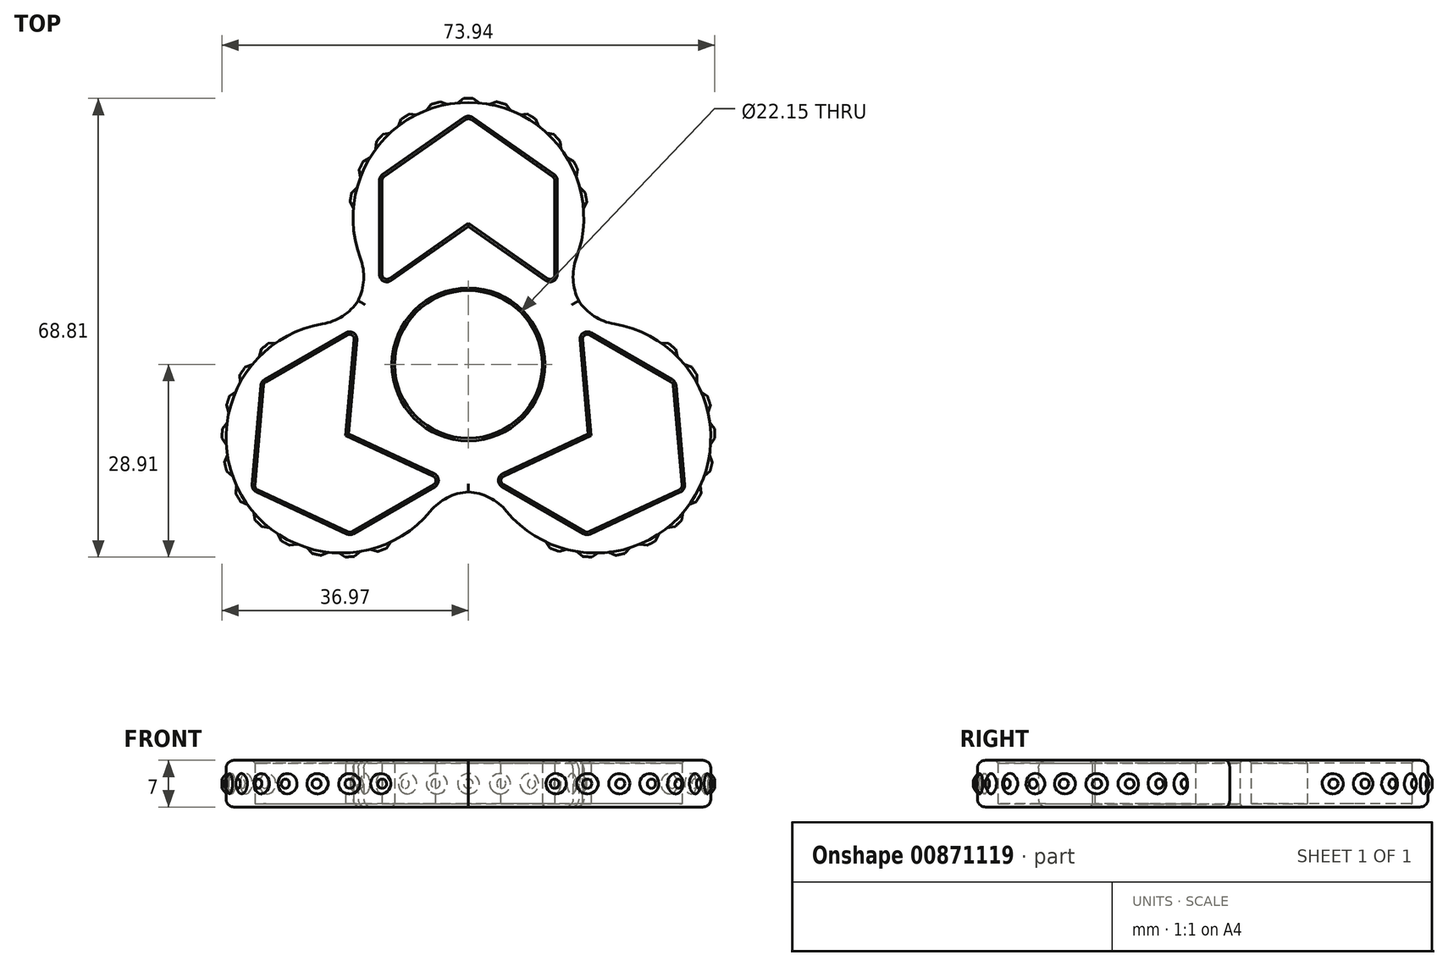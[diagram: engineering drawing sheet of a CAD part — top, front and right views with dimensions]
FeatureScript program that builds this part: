
annotation { "Feature Type Name" : "Feature", "Feature Type Description" : "" }
export const myFeature = defineFeature(function(context is Context, id is Id, definition is map)
    precondition{}
    {
        {
            var Q0;
            Q0=qCreatedBy(makeId("Top.planeOp"),FACE);
            var sketch = newSketch(context, id + "F0", { "sketchPlane" : qUnion([Q0])});
            skCircle(sketch, "E0", {"center": v(0, 0) * mm, "radius": 11.07 * mm});
            skCircle(sketch, "E1", {"center": v(0, 0) * mm, "radius": 26.5 * mm, "construction": true});
            skArc(sketch, "E2", {"start": v(-13.1, 23.03) * mm, "mid": v(-13.03, 22.75) * mm, "end": v(-12.95, 22.47) * mm, "construction": true});
            skLineSegment(sketch, "E3", {"start": v(0, 43.45) * mm, "end": v(0, 0) * mm});
            skLineSegment(sketch, "E4", {"start": v(0, 37) * mm, "end": v(12.95, 27.94) * mm});
            skLineSegment(sketch, "E5", {"start": v(12.95, 27.94) * mm, "end": v(12.95, 12.13) * mm});
            skLineSegment(sketch, "E6", {"start": v(12.95, 12.13) * mm, "end": v(0, 21.2) * mm});
            skLineSegment(sketch, "E7.MirrorCS", {"start": v(0, 37) * mm, "end": v(-12.95, 27.94) * mm});
            skLineSegment(sketch, "E8.MirrorCS", {"start": v(-12.95, 27.94) * mm, "end": v(-12.95, 12.13) * mm});
            skLineSegment(sketch, "E9.MirrorCS", {"start": v(-12.95, 12.13) * mm, "end": v(0, 21.2) * mm});
            skLineSegment(sketch, "E10.1.0", {"start": v(-32.1, -18.57) * mm, "end": v(-17.76, -25.25) * mm});
            skLineSegment(sketch, "E10.1.1", {"start": v(-17.76, -25.25) * mm, "end": v(-4.07, -17.35) * mm});
            skLineSegment(sketch, "E10.1.2", {"start": v(-4.07, -17.35) * mm, "end": v(-18.4, -10.67) * mm});
            skLineSegment(sketch, "E10.1.3", {"start": v(-17.02, 5.08) * mm, "end": v(-18.4, -10.67) * mm});
            skLineSegment(sketch, "E10.1.4", {"start": v(-30.71, -2.82) * mm, "end": v(-17.02, 5.08) * mm});
            skLineSegment(sketch, "E10.1.5", {"start": v(-32.1, -18.57) * mm, "end": v(-30.71, -2.82) * mm});
            skLineSegment(sketch, "E10.2.0", {"start": v(32.1, -18.57) * mm, "end": v(30.71, -2.82) * mm});
            skLineSegment(sketch, "E10.2.1", {"start": v(30.71, -2.82) * mm, "end": v(17.02, 5.08) * mm});
            skLineSegment(sketch, "E10.2.2", {"start": v(17.02, 5.08) * mm, "end": v(18.4, -10.67) * mm});
            skLineSegment(sketch, "E10.2.3", {"start": v(4.07, -17.35) * mm, "end": v(18.4, -10.67) * mm});
            skLineSegment(sketch, "E10.2.4", {"start": v(17.76, -25.25) * mm, "end": v(4.07, -17.35) * mm});
            skLineSegment(sketch, "E10.2.5", {"start": v(32.1, -18.57) * mm, "end": v(17.76, -25.25) * mm});
            skPoint(sketch, "E10.center", {"position": v(0, -0.05) * mm});
            skArc(sketch, "E11.trimOffspring", {"start": v(12.95, 22.47) * mm, "mid": v(13, 22.77) * mm, "end": v(13.05, 23.06) * mm, "construction": true});
            skCircle(sketch, "E12", {"center": v(0, 22) * mm, "radius": 17.3 * mm});
            skCircle(sketch, "E13.1.0", {"center": v(-19.05, -11) * mm, "radius": 17.3 * mm});
            skCircle(sketch, "E13.2.0", {"center": v(19.05, -11) * mm, "radius": 17.3 * mm});
            skLineSegment(sketch, "E14", {"start": v(-17.02, 5.08) * mm, "end": v(-12.95, 12.13) * mm});
            skLineSegment(sketch, "E15", {"start": v(12.95, 12.13) * mm, "end": v(17.02, 5.08) * mm});
            skLineSegment(sketch, "E16", {"start": v(4.07, -17.35) * mm, "end": v(-4.07, -17.35) * mm});
            skLineSegment(sketch, "E17", {"start": v(-7.18, -19.14) * mm, "end": v(7.18, -19.14) * mm});
            skLineSegment(sketch, "E18.1.0", {"start": v(20.13, 3.3) * mm, "end": v(12.96, 15.73) * mm});
            skLineSegment(sketch, "E18.2.0", {"start": v(-12.96, 15.73) * mm, "end": v(-20.13, 3.3) * mm});
            skPoint(sketch, "E18.center", {"position": v(0, -0.03) * mm});
            skSolve(sketch);
        }
        {
            var Q0;
            {var subQ1=sQuery(id+"F0.wireOp",EDGE,"E7.MirrorCS");Q0=makeQuery(id+"F0.imprint","IMPRINT",FACE,{"disambiguationData":[TD([[makeQuery(id+"F0.imprint","IMPRINT",EDGE,{"derivedFrom":subQ1}),-1.0]])]});}
            var Q1;
            {var subQ0=sQuery(id+"F0.wireOp",EDGE,"E4");Q1=makeQuery(id+"F0.imprint","IMPRINT",FACE,{"disambiguationData":[TD([[makeQuery(id+"F0.imprint","IMPRINT",EDGE,{"derivedFrom":subQ0}),1.0]])]});}
            var Q2;
            {var subQ5=sQuery(id+"F0.wireOp",EDGE,"E6");Q2=makeQuery(id+"F0.imprint","IMPRINT",FACE,{"disambiguationData":[TD([[makeQuery(id+"F0.imprint","IMPRINT",EDGE,{"derivedFrom":subQ5}),1.0]])]});}
            var Q3;
            {var subQ0=sQuery(id+"F0.wireOp",EDGE,"E9.MirrorCS");Q3=makeQuery(id+"F0.imprint","IMPRINT",FACE,{"disambiguationData":[TD([[makeQuery(id+"F0.imprint","IMPRINT",EDGE,{"derivedFrom":subQ0}),-1.0]])]});}
            var Q4;
            {var subQ0=sQuery(id+"F0.wireOp",EDGE,"E12");var subQ1=sQuery(id+"F0.wireOp",EDGE,"E0");var subQ2=makeQuery(id+"F0.imprint","INTERSECT",VERTEX,{"disambiguationData":[OD(1.0)],"derivedFrom":[subQ1,subQ0]});Q4=makeQuery(id+"F0.imprint","IMPRINT",FACE,{"disambiguationData":[TD([[makeQuery(id+"F0.imprint","IMPRINT",EDGE,{"disambiguationData":[TD([[subQ2,-1.0]])],"derivedFrom":subQ1}),-1.0]])]});}
            var Q5;
            {var subQ1=sQuery(id+"F0.wireOp",EDGE,"E10.1.2");Q5=makeQuery(id+"F0.imprint","IMPRINT",FACE,{"disambiguationData":[TD([[makeQuery(id+"F0.imprint","IMPRINT",EDGE,{"derivedFrom":subQ1}),-1.0]])]});}
            var Q6;
            {var subQ0=sQuery(id+"F0.wireOp",EDGE,"E13.1.0");var subQ1=sQuery(id+"F0.wireOp",EDGE,"E0");var subQ2=makeQuery(id+"F0.imprint","INTERSECT",VERTEX,{"disambiguationData":[OD(1.0)],"derivedFrom":[subQ1,subQ0]});Q6=makeQuery(id+"F0.imprint","IMPRINT",FACE,{"disambiguationData":[TD([[makeQuery(id+"F0.imprint","IMPRINT",EDGE,{"disambiguationData":[TD([[subQ2,-1.0]])],"derivedFrom":subQ1}),-1.0]])]});}
            var Q7;
            {var subQ9=sQuery(id+"F0.wireOp",EDGE,"E10.2.2");Q7=makeQuery(id+"F0.imprint","IMPRINT",FACE,{"disambiguationData":[TD([[makeQuery(id+"F0.imprint","IMPRINT",EDGE,{"derivedFrom":subQ9}),-1.0]])]});}
            var Q8;
            {var subQ0=sQuery(id+"F0.wireOp",EDGE,"E12");var subQ1=sQuery(id+"F0.wireOp",EDGE,"E0");var subQ2=makeQuery(id+"F0.imprint","INTERSECT",VERTEX,{"disambiguationData":[OD(0.0)],"derivedFrom":[subQ1,subQ0]});Q8=makeQuery(id+"F0.imprint","IMPRINT",FACE,{"disambiguationData":[TD([[makeQuery(id+"F0.imprint","IMPRINT",EDGE,{"disambiguationData":[TD([[subQ2,1.0]])],"derivedFrom":subQ1}),-1.0]])]});}
            var Q9;
            {var subQ6=sQuery(id+"F0.wireOp",EDGE,"E10.2.0");Q9=makeQuery(id+"F0.imprint","IMPRINT",FACE,{"disambiguationData":[TD([[makeQuery(id+"F0.imprint","IMPRINT",EDGE,{"derivedFrom":subQ6}),-1.0]])]});}
            var Q10;
            {var subQ7=sQuery(id+"F0.wireOp",EDGE,"E10.1.0");Q10=makeQuery(id+"F0.imprint","IMPRINT",FACE,{"disambiguationData":[TD([[makeQuery(id+"F0.imprint","IMPRINT",EDGE,{"derivedFrom":subQ7}),-1.0]])]});}
            var Q11;
            {var subQ0=sQuery(id+"F0.wireOp",EDGE,"E18.2.0");var subQ1=sQuery(id+"F0.wireOp",EDGE,"E12");var subQ2=makeQuery(id+"F0.imprint","INTERSECT",VERTEX,{"derivedFrom":[subQ1,subQ0]});Q11=makeQuery(id+"F0.imprint","IMPRINT",FACE,{"disambiguationData":[TD([[makeQuery(id+"F0.imprint","IMPRINT",EDGE,{"disambiguationData":[TD([[subQ2,-1.0]])],"derivedFrom":subQ1}),-1.0]])]});}
            var Q12;
            {var subQ0=sQuery(id+"F0.wireOp",EDGE,"E17");var subQ1=sQuery(id+"F0.wireOp",EDGE,"E13.1.0");var subQ2=makeQuery(id+"F0.imprint","INTERSECT",VERTEX,{"derivedFrom":[subQ1,subQ0]});Q12=makeQuery(id+"F0.imprint","IMPRINT",FACE,{"disambiguationData":[TD([[makeQuery(id+"F0.imprint","IMPRINT",EDGE,{"disambiguationData":[TD([[subQ2,-1.0]])],"derivedFrom":subQ1}),-1.0]])]});}
            var Q13;
            {var subQ3=sQuery(id+"F0.wireOp",EDGE,"E18.2.0");var subQ5=sQuery(id+"F0.wireOp",EDGE,"E12");var subQ7=makeQuery(id+"F0.imprint","INTERSECT",VERTEX,{"derivedFrom":[subQ5,subQ3]});Q13=makeQuery(id+"F0.imprint","IMPRINT",FACE,{"disambiguationData":[TD([[makeQuery(id+"F0.imprint","IMPRINT",EDGE,{"disambiguationData":[TD([[subQ7,-1.0]])],"derivedFrom":subQ5}),1.0]])]});}
            var Q14;
            {var subQ3=sQuery(id+"F0.wireOp",EDGE,"E18.2.0");var subQ5=sQuery(id+"F0.wireOp",EDGE,"E13.1.0");var subQ7=makeQuery(id+"F0.imprint","INTERSECT",VERTEX,{"derivedFrom":[subQ5,subQ3]});Q14=makeQuery(id+"F0.imprint","IMPRINT",FACE,{"disambiguationData":[TD([[makeQuery(id+"F0.imprint","IMPRINT",EDGE,{"disambiguationData":[TD([[subQ7,1.0]])],"derivedFrom":subQ5}),1.0]])]});}
            var Q15;
            {var subQ3=sQuery(id+"F0.wireOp",EDGE,"E17");var subQ5=sQuery(id+"F0.wireOp",EDGE,"E13.1.0");var subQ6=makeQuery(id+"F0.imprint","INTERSECT",VERTEX,{"derivedFrom":[subQ5,subQ3]});Q15=makeQuery(id+"F0.imprint","IMPRINT",FACE,{"disambiguationData":[TD([[makeQuery(id+"F0.imprint","IMPRINT",EDGE,{"disambiguationData":[TD([[subQ6,-1.0]])],"derivedFrom":subQ5}),1.0]])]});}
            var Q16;
            {var subQ3=sQuery(id+"F0.wireOp",EDGE,"E17");var subQ5=sQuery(id+"F0.wireOp",EDGE,"E13.2.0");var subQ6=makeQuery(id+"F0.imprint","INTERSECT",VERTEX,{"derivedFrom":[subQ5,subQ3]});Q16=makeQuery(id+"F0.imprint","IMPRINT",FACE,{"disambiguationData":[TD([[makeQuery(id+"F0.imprint","IMPRINT",EDGE,{"disambiguationData":[TD([[subQ6,1.0]])],"derivedFrom":subQ5}),1.0]])]});}
            var Q17;
            {var subQ3=sQuery(id+"F0.wireOp",EDGE,"E18.1.0");var subQ5=sQuery(id+"F0.wireOp",EDGE,"E12");var subQ7=makeQuery(id+"F0.imprint","INTERSECT",VERTEX,{"derivedFrom":[subQ5,subQ3]});Q17=makeQuery(id+"F0.imprint","IMPRINT",FACE,{"disambiguationData":[TD([[makeQuery(id+"F0.imprint","IMPRINT",EDGE,{"disambiguationData":[TD([[subQ7,1.0]])],"derivedFrom":subQ5}),1.0]])]});}
            var Q18;
            {var subQ3=sQuery(id+"F0.wireOp",EDGE,"E18.1.0");var subQ5=sQuery(id+"F0.wireOp",EDGE,"E13.2.0");var subQ6=makeQuery(id+"F0.imprint","INTERSECT",VERTEX,{"derivedFrom":[subQ5,subQ3]});Q18=makeQuery(id+"F0.imprint","IMPRINT",FACE,{"disambiguationData":[TD([[makeQuery(id+"F0.imprint","IMPRINT",EDGE,{"disambiguationData":[TD([[subQ6,-1.0]])],"derivedFrom":subQ5}),1.0]])]});}
            var Q19;
            {var subQ0=sQuery(id+"F0.wireOp",EDGE,"E18.1.0");var subQ1=sQuery(id+"F0.wireOp",EDGE,"E12");var subQ2=makeQuery(id+"F0.imprint","INTERSECT",VERTEX,{"derivedFrom":[subQ1,subQ0]});Q19=makeQuery(id+"F0.imprint","IMPRINT",FACE,{"disambiguationData":[TD([[makeQuery(id+"F0.imprint","IMPRINT",EDGE,{"disambiguationData":[TD([[subQ2,1.0]])],"derivedFrom":subQ1}),-1.0]])]});}
            extrude(context, id + "F1", {"entities" : qUnion([Q0, Q1, Q2, Q3, Q4, Q5, Q6, Q7, Q8, Q9, Q10, Q11, Q12, Q13, Q14, Q15, Q16, Q17, Q18, Q19]), "depth" : 7 * mm, "offsetDistance" : 25 * mm});
        }
        {
            var Q0;
            {var subQ1=sQuery(id+"F0.wireOp",EDGE,"E4");Q0=makeQuery(id+"F0.imprint","IMPRINT",FACE,{"disambiguationData":[TD([[makeQuery(id+"F0.imprint","IMPRINT",EDGE,{"derivedFrom":subQ1}),-1.0]])]});}
            var Q1;
            {var subQ3=sQuery(id+"F0.wireOp",EDGE,"E7.MirrorCS");Q1=makeQuery(id+"F0.imprint","IMPRINT",FACE,{"disambiguationData":[TD([[makeQuery(id+"F0.imprint","IMPRINT",EDGE,{"derivedFrom":subQ3}),1.0]])]});}
            var Q2;
            {var subQ3=sQuery(id+"F0.wireOp",EDGE,"E10.2.0");Q2=makeQuery(id+"F0.imprint","IMPRINT",FACE,{"disambiguationData":[TD([[makeQuery(id+"F0.imprint","IMPRINT",EDGE,{"derivedFrom":subQ3}),1.0]])]});}
            var Q3;
            {var subQ3=sQuery(id+"F0.wireOp",EDGE,"E10.1.0");Q3=makeQuery(id+"F0.imprint","IMPRINT",FACE,{"disambiguationData":[TD([[makeQuery(id+"F0.imprint","IMPRINT",EDGE,{"derivedFrom":subQ3}),1.0]])]});}
            extrude(context, id + "F2", {"entities" : qUnion([Q0, Q1, Q2, Q3]), "operationType" : NewBodyOperationType.ADD, "depth" : 0.5 * mm, "offsetDistance" : 25 * mm});
        }
        {
            var Q0;
            Q0=makeQuery(id+"F1.opExtrude","SWEPT_EDGE",EDGE,{"disambiguationData":[OSD([sQuery(id+"F0.wireOp",EDGE,"E12"),sQuery(id+"F0.wireOp",EDGE,"Zo6cloxw-RQWd-VoTV-Hmrh-WUM4IXPVoAln")])]});
            var Q1;
            Q1=makeQuery(id+"F1.opExtrude","SWEPT_EDGE",EDGE,{"disambiguationData":[OSD([sQuery(id+"F0.wireOp",EDGE,"E13.1.0"),sQuery(id+"F0.wireOp",EDGE,"Zo6cloxw-RQWd-VoTV-Hmrh-WUM4IXPVoAln")])]});
            var Q2;
            Q2=makeQuery(id+"F1.opExtrude","SWEPT_EDGE",EDGE,{"disambiguationData":[OSD([sQuery(id+"F0.wireOp",EDGE,"E13.2.0"),sQuery(id+"F0.wireOp",EDGE,"qCIH2ttQ-GXot-xXQ0-Qejf-B46ZgPa41a3F")])]});
            var Q3;
            Q3=makeQuery(id+"F1.opExtrude","SWEPT_EDGE",EDGE,{"disambiguationData":[OSD([sQuery(id+"F0.wireOp",EDGE,"E12"),sQuery(id+"F0.wireOp",EDGE,"qCIH2ttQ-GXot-xXQ0-Qejf-B46ZgPa41a3F")])]});
            var Q4;
            Q4=makeQuery(id+"F1.opExtrude","SWEPT_EDGE",EDGE,{"disambiguationData":[OSD([sQuery(id+"F0.wireOp",EDGE,"E13.2.0"),sQuery(id+"F0.wireOp",EDGE,"L0YcY93C-S2HS-15lv-KyWX-i7wwrRtpjOze")])]});
            var Q5;
            Q5=makeQuery(id+"F1.opExtrude","SWEPT_EDGE",EDGE,{"disambiguationData":[OSD([sQuery(id+"F0.wireOp",EDGE,"E13.1.0"),sQuery(id+"F0.wireOp",EDGE,"L0YcY93C-S2HS-15lv-KyWX-i7wwrRtpjOze")])]});
            fillet(context, id + "F3", {"entities" : qUnion([Q0, Q1, Q2, Q3, Q4, Q5]), "radius" : 8 * mm, "tangentPropagation" : true, "allowEdgeOverflow" : false});
        }
        {
            var Q0;
            Q0=makeQuery(id+"F1.opExtrude","CAP_EDGE",EDGE,{"disambiguationData":[OSD([sQuery(id+"F0.wireOp",EDGE,"E13.2.0")])],"isStart":true});
            var Q1;
            Q1=makeQuery(id+"F1.opExtrude","CAP_EDGE",EDGE,{"disambiguationData":[OSD([sQuery(id+"F0.wireOp",EDGE,"E13.1.0")])],"isStart":true});
            var Q2;
            Q2=makeQuery(id+"F1.opExtrude","CAP_EDGE",EDGE,{"disambiguationData":[OSD([sQuery(id+"F0.wireOp",EDGE,"E12")])],"isStart":true});
            var Q3;
            Q3=makeQuery(id+"F1.opExtrude","CAP_EDGE",EDGE,{"disambiguationData":[OSD([sQuery(id+"F0.wireOp",EDGE,"E12")])],"isStart":false});
            var Q4;
            Q4=makeQuery(id+"F1.opExtrude","CAP_EDGE",EDGE,{"disambiguationData":[OSD([sQuery(id+"F0.wireOp",EDGE,"E13.2.0")])],"isStart":false});
            var Q5;
            Q5=makeQuery(id+"F1.opExtrude","CAP_EDGE",EDGE,{"disambiguationData":[OSD([sQuery(id+"F0.wireOp",EDGE,"E13.1.0")])],"isStart":false});
            fillet(context, id + "F4", {"entities" : qUnion([Q0, Q1, Q2, Q3, Q4, Q5]), "radius" : 1.2 * mm, "tangentPropagation" : true, "allowEdgeOverflow" : false});
        }
        {
            var Q0;
            Q0=makeQuery(id+"F1.opExtrude","SWEPT_EDGE",EDGE,{"disambiguationData":[OSD([sQuery(id+"F0.wireOp",EDGE,"E10.1.0"),sQuery(id+"F0.wireOp",EDGE,"E10.1.5")])]});
            var Q1;
            Q1=makeQuery(id+"F1.opExtrude","SWEPT_EDGE",EDGE,{"disambiguationData":[OSD([sQuery(id+"F0.wireOp",EDGE,"E10.1.1"),sQuery(id+"F0.wireOp",EDGE,"E10.1.2"),sQuery(id+"F0.wireOp",EDGE,"L0YcY93C-S2HS-15lv-KyWX-i7wwrRtpjOze")])]});
            var Q2;
            Q2=makeQuery(id+"F1.opExtrude","SWEPT_EDGE",EDGE,{"disambiguationData":[OSD([sQuery(id+"F0.wireOp",EDGE,"E10.1.3"),sQuery(id+"F0.wireOp",EDGE,"E10.1.4"),sQuery(id+"F0.wireOp",EDGE,"Zo6cloxw-RQWd-VoTV-Hmrh-WUM4IXPVoAln")])]});
            var Q3;
            Q3=makeQuery(id+"F1.opExtrude","SWEPT_EDGE",EDGE,{"disambiguationData":[OSD([sQuery(id+"F0.wireOp",EDGE,"E10.1.0"),sQuery(id+"F0.wireOp",EDGE,"E10.1.1")])]});
            var Q4;
            Q4=makeQuery(id+"F1.opExtrude","SWEPT_EDGE",EDGE,{"disambiguationData":[OSD([sQuery(id+"F0.wireOp",EDGE,"E10.1.4"),sQuery(id+"F0.wireOp",EDGE,"E10.1.5")])]});
            var Q5;
            Q5=makeQuery(id+"F1.opExtrude","SWEPT_EDGE",EDGE,{"disambiguationData":[OSD([sQuery(id+"F0.wireOp",EDGE,"E10.2.3"),sQuery(id+"F0.wireOp",EDGE,"E10.2.4"),sQuery(id+"F0.wireOp",EDGE,"L0YcY93C-S2HS-15lv-KyWX-i7wwrRtpjOze")])]});
            var Q6;
            Q6=makeQuery(id+"F1.opExtrude","SWEPT_EDGE",EDGE,{"disambiguationData":[OSD([sQuery(id+"F0.wireOp",EDGE,"E10.2.4"),sQuery(id+"F0.wireOp",EDGE,"E10.2.5")])]});
            var Q7;
            Q7=makeQuery(id+"F1.opExtrude","SWEPT_EDGE",EDGE,{"disambiguationData":[OSD([sQuery(id+"F0.wireOp",EDGE,"E10.2.0"),sQuery(id+"F0.wireOp",EDGE,"E10.2.5")])]});
            var Q8;
            Q8=makeQuery(id+"F1.opExtrude","SWEPT_EDGE",EDGE,{"disambiguationData":[OSD([sQuery(id+"F0.wireOp",EDGE,"E10.2.0"),sQuery(id+"F0.wireOp",EDGE,"E10.2.1")])]});
            var Q9;
            Q9=makeQuery(id+"F1.opExtrude","SWEPT_EDGE",EDGE,{"disambiguationData":[OSD([sQuery(id+"F0.wireOp",EDGE,"E10.2.1"),sQuery(id+"F0.wireOp",EDGE,"E10.2.2"),sQuery(id+"F0.wireOp",EDGE,"qCIH2ttQ-GXot-xXQ0-Qejf-B46ZgPa41a3F")])]});
            var Q10;
            Q10=makeQuery(id+"F1.opExtrude","SWEPT_EDGE",EDGE,{"disambiguationData":[OSD([sQuery(id+"F0.wireOp",EDGE,"E5"),sQuery(id+"F0.wireOp",EDGE,"E6"),sQuery(id+"F0.wireOp",EDGE,"qCIH2ttQ-GXot-xXQ0-Qejf-B46ZgPa41a3F")])]});
            var Q11;
            Q11=makeQuery(id+"F1.opExtrude","SWEPT_EDGE",EDGE,{"disambiguationData":[OSD([sQuery(id+"F0.wireOp",EDGE,"E8.MirrorCS"),sQuery(id+"F0.wireOp",EDGE,"E9.MirrorCS"),sQuery(id+"F0.wireOp",EDGE,"Zo6cloxw-RQWd-VoTV-Hmrh-WUM4IXPVoAln")])]});
            var Q12;
            Q12=makeQuery(id+"F1.opExtrude","SWEPT_EDGE",EDGE,{"disambiguationData":[OSD([sQuery(id+"F0.wireOp",EDGE,"E4"),sQuery(id+"F0.wireOp",EDGE,"E5")])]});
            var Q13;
            Q13=makeQuery(id+"F1.opExtrude","SWEPT_EDGE",EDGE,{"disambiguationData":[OSD([sQuery(id+"F0.wireOp",EDGE,"E3"),sQuery(id+"F0.wireOp",EDGE,"E4"),sQuery(id+"F0.wireOp",EDGE,"E7.MirrorCS")])]});
            var Q14;
            Q14=makeQuery(id+"F1.opExtrude","SWEPT_EDGE",EDGE,{"disambiguationData":[OSD([sQuery(id+"F0.wireOp",EDGE,"E7.MirrorCS"),sQuery(id+"F0.wireOp",EDGE,"E8.MirrorCS")])]});
            fillet(context, id + "F5", {"entities" : qUnion([Q0, Q1, Q2, Q3, Q4, Q5, Q6, Q7, Q8, Q9, Q10, Q11, Q12, Q13, Q14]), "radius" : 0.7 * mm, "tangentPropagation" : true, "allowEdgeOverflow" : false});
        }
        {
            var Q0;
            Q0=makeQuery(id+"F1.opExtrude","CAP_FACE",FACE,{"disambiguationData":[OSD([sQuery(id+"F0.wireOp",EDGE,"E0"),sQuery(id+"F0.wireOp",EDGE,"E4"),sQuery(id+"F0.wireOp",EDGE,"E5"),sQuery(id+"F0.wireOp",EDGE,"E6"),sQuery(id+"F0.wireOp",EDGE,"E7.MirrorCS"),sQuery(id+"F0.wireOp",EDGE,"E8.MirrorCS"),sQuery(id+"F0.wireOp",EDGE,"E9.MirrorCS"),sQuery(id+"F0.wireOp",EDGE,"E10.1.0"),sQuery(id+"F0.wireOp",EDGE,"E10.1.1"),sQuery(id+"F0.wireOp",EDGE,"E10.1.2"),sQuery(id+"F0.wireOp",EDGE,"E10.1.3"),sQuery(id+"F0.wireOp",EDGE,"E10.1.4"),sQuery(id+"F0.wireOp",EDGE,"E10.1.5"),sQuery(id+"F0.wireOp",EDGE,"E10.2.0"),sQuery(id+"F0.wireOp",EDGE,"E10.2.1"),sQuery(id+"F0.wireOp",EDGE,"E10.2.2"),sQuery(id+"F0.wireOp",EDGE,"E10.2.3"),sQuery(id+"F0.wireOp",EDGE,"E10.2.4"),sQuery(id+"F0.wireOp",EDGE,"E10.2.5"),sQuery(id+"F0.wireOp",EDGE,"E12"),sQuery(id+"F0.wireOp",EDGE,"E13.1.0"),sQuery(id+"F0.wireOp",EDGE,"E13.2.0"),sQuery(id+"F0.wireOp",EDGE,"qCIH2ttQ-GXot-xXQ0-Qejf-B46ZgPa41a3F"),sQuery(id+"F0.wireOp",EDGE,"Zo6cloxw-RQWd-VoTV-Hmrh-WUM4IXPVoAln"),sQuery(id+"F0.wireOp",EDGE,"L0YcY93C-S2HS-15lv-KyWX-i7wwrRtpjOze")])],"isStart":true});
            var Q1;
            Q1=makeQuery(id+"F1.opExtrude","CAP_FACE",FACE,{"disambiguationData":[OSD([sQuery(id+"F0.wireOp",EDGE,"E0"),sQuery(id+"F0.wireOp",EDGE,"E4"),sQuery(id+"F0.wireOp",EDGE,"E5"),sQuery(id+"F0.wireOp",EDGE,"E6"),sQuery(id+"F0.wireOp",EDGE,"E7.MirrorCS"),sQuery(id+"F0.wireOp",EDGE,"E8.MirrorCS"),sQuery(id+"F0.wireOp",EDGE,"E9.MirrorCS"),sQuery(id+"F0.wireOp",EDGE,"E10.1.0"),sQuery(id+"F0.wireOp",EDGE,"E10.1.1"),sQuery(id+"F0.wireOp",EDGE,"E10.1.2"),sQuery(id+"F0.wireOp",EDGE,"E10.1.3"),sQuery(id+"F0.wireOp",EDGE,"E10.1.4"),sQuery(id+"F0.wireOp",EDGE,"E10.1.5"),sQuery(id+"F0.wireOp",EDGE,"E10.2.0"),sQuery(id+"F0.wireOp",EDGE,"E10.2.1"),sQuery(id+"F0.wireOp",EDGE,"E10.2.2"),sQuery(id+"F0.wireOp",EDGE,"E10.2.3"),sQuery(id+"F0.wireOp",EDGE,"E10.2.4"),sQuery(id+"F0.wireOp",EDGE,"E10.2.5"),sQuery(id+"F0.wireOp",EDGE,"E12"),sQuery(id+"F0.wireOp",EDGE,"E13.1.0"),sQuery(id+"F0.wireOp",EDGE,"E13.2.0"),sQuery(id+"F0.wireOp",EDGE,"qCIH2ttQ-GXot-xXQ0-Qejf-B46ZgPa41a3F"),sQuery(id+"F0.wireOp",EDGE,"Zo6cloxw-RQWd-VoTV-Hmrh-WUM4IXPVoAln"),sQuery(id+"F0.wireOp",EDGE,"L0YcY93C-S2HS-15lv-KyWX-i7wwrRtpjOze")])],"isStart":false});
            chamfer(context, id + "F6", {"entities" : qUnion([Q0, Q1]), "width" : 0.4 * mm, "tangentPropagation" : true});
        }
        {
            var Q0;
            {var subQ0=sQuery(id+"F0.wireOp",EDGE,"E12");Q0=makeQuery(id+"F4.opFillet","BLEND_EDGE",EDGE,{"blendedFrom":[makeQuery(id+"F1.opExtrude","CAP_EDGE",EDGE,{"disambiguationData":[OSD([subQ0])],"isStart":true}),makeQuery(id+"F1.opExtrude","SWEPT_FACE",FACE,{"disambiguationData":[OSD([subQ0])]})],"blendedInto":[makeQuery(id+"F1.opExtrude","SWEPT_FACE",FACE,{"disambiguationData":[OSD([subQ0])]})]});}
            cPoint(context, id + "F7", {"entities" : qUnion([Q0]), "parameter" : 0.5});
        }
        {
            var Q0;
            Q0=qCreatedBy(makeId("Front.planeOp"),FACE);
            var Q1;
            Q1 = qCreatedBy(id + "F7" ,VERTEX);
            cPlane(context, id + "F8", {"entities" : qUnion([Q0, Q1]), "cplaneType" : CPlaneType.PLANE_POINT, "offset" : 25 * mm, "width" : 150 * mm, "height" : 150 * mm});
        }
        {
            var Q0;
            Q0=qCreatedBy(id+"F8.planeOp",FACE);
            var sketch = newSketch(context, id + "F9", { "sketchPlane" : qUnion([Q0])});
            skCircle(sketch, "E19", {"center": v(0, 3.5) * mm, "radius": 1.8 * mm});
            skSolve(sketch);
        }
        {
            var Q0;
            Q0=makeQuery(id+"F9.imprint","IMPRINT",FACE,{"disambiguationData":[TD([[makeQuery(id+"F9.imprint","IMPRINT",EDGE,{"derivedFrom":sQuery(id+"F9.wireOp",EDGE,"E19")}),1.0]])]});
            var Q1;
            Q1=sQuery(id+"F9.wireOp",EDGE,"E19");
            extrude(context, id + "F10", {"entities" : qUnion([Q0]), "surfaceEntities" : qUnion([Q1]), "oppositeDirection" : true, "depth" : 0.6 * mm, "offsetDistance" : 25 * mm, "hasSecondDirection" : true, "secondDirectionOppositeDirection" : false, "secondDirectionDepth" : 0.4 * mm});
        }
        {
            var Q0;
            Q0=makeQuery(id+"F10.opExtrude","CAP_EDGE",EDGE,{"disambiguationData":[OSD([sQuery(id+"F9.wireOp",EDGE,"E19")])],"isStart":false});
            chamfer(context, id + "F11", {"entities" : qUnion([Q0]), "chamferType" : ChamferType.TWO_OFFSETS, "width1" : 0.8 * mm, "oppositeDirection" : false, "width2" : 1.1 * mm, "tangentPropagation" : true});
        }
        {
            var Q0;
            Q0=makeQuery(id+"F10.opExtrude","SWEPT_BODY",BODY,{"disambiguationData":[OSD([sQuery(id+"F9.wireOp",EDGE,"E19")])]});
            var Q1;
            Q1=makeQuery(id+"F1.opExtrude","SWEPT_FACE",FACE,{"disambiguationData":[OSD([sQuery(id+"F0.wireOp",EDGE,"E12")])]});
            circularPattern(context, id + "F12", {"entities" : qUnion([Q0]), "axis" : qUnion([Q1]), "angle" : 80 * degree, "instanceCount" : 6, "equalSpace" : true, "isCentered" : true});
        }
        {
            var Q0;
            Q0=makeQuery(id+"F10.opExtrude","SWEPT_BODY",BODY,{"disambiguationData":[OSD([sQuery(id+"F9.wireOp",EDGE,"E19")])]});
            var Q1;
            Q1=makeQuery(id+"F12.opPattern","COPY",BODY,{"derivedFrom":makeQuery(id+"F10.opExtrude","SWEPT_BODY",BODY,{"disambiguationData":[OSD([sQuery(id+"F9.wireOp",EDGE,"E19")])]}),"instanceName":"-8"});
            var Q2;
            Q2=makeQuery(id+"F12.opPattern","COPY",BODY,{"derivedFrom":makeQuery(id+"F10.opExtrude","SWEPT_BODY",BODY,{"disambiguationData":[OSD([sQuery(id+"F9.wireOp",EDGE,"E19")])]}),"instanceName":"-7"});
            var Q3;
            Q3=makeQuery(id+"F12.opPattern","COPY",BODY,{"derivedFrom":makeQuery(id+"F10.opExtrude","SWEPT_BODY",BODY,{"disambiguationData":[OSD([sQuery(id+"F9.wireOp",EDGE,"E19")])]}),"instanceName":"-6"});
            var Q4;
            Q4=makeQuery(id+"F12.opPattern","COPY",BODY,{"derivedFrom":makeQuery(id+"F10.opExtrude","SWEPT_BODY",BODY,{"disambiguationData":[OSD([sQuery(id+"F9.wireOp",EDGE,"E19")])]}),"instanceName":"-5"});
            var Q5;
            Q5=makeQuery(id+"F12.opPattern","COPY",BODY,{"derivedFrom":makeQuery(id+"F10.opExtrude","SWEPT_BODY",BODY,{"disambiguationData":[OSD([sQuery(id+"F9.wireOp",EDGE,"E19")])]}),"instanceName":"-4"});
            var Q6;
            Q6=makeQuery(id+"F12.opPattern","COPY",BODY,{"derivedFrom":makeQuery(id+"F10.opExtrude","SWEPT_BODY",BODY,{"disambiguationData":[OSD([sQuery(id+"F9.wireOp",EDGE,"E19")])]}),"instanceName":"-3"});
            var Q7;
            Q7=makeQuery(id+"F12.opPattern","COPY",BODY,{"derivedFrom":makeQuery(id+"F10.opExtrude","SWEPT_BODY",BODY,{"disambiguationData":[OSD([sQuery(id+"F9.wireOp",EDGE,"E19")])]}),"instanceName":"-2"});
            var Q8;
            Q8=makeQuery(id+"F12.opPattern","COPY",BODY,{"derivedFrom":makeQuery(id+"F10.opExtrude","SWEPT_BODY",BODY,{"disambiguationData":[OSD([sQuery(id+"F9.wireOp",EDGE,"E19")])]}),"instanceName":"-1"});
            var Q9;
            Q9=makeQuery(id+"F12.opPattern","COPY",BODY,{"derivedFrom":makeQuery(id+"F10.opExtrude","SWEPT_BODY",BODY,{"disambiguationData":[OSD([sQuery(id+"F9.wireOp",EDGE,"E19")])]}),"instanceName":"1"});
            var Q10;
            Q10=makeQuery(id+"F12.opPattern","COPY",BODY,{"derivedFrom":makeQuery(id+"F10.opExtrude","SWEPT_BODY",BODY,{"disambiguationData":[OSD([sQuery(id+"F9.wireOp",EDGE,"E19")])]}),"instanceName":"2"});
            var Q11;
            Q11=makeQuery(id+"F12.opPattern","COPY",BODY,{"derivedFrom":makeQuery(id+"F10.opExtrude","SWEPT_BODY",BODY,{"disambiguationData":[OSD([sQuery(id+"F9.wireOp",EDGE,"E19")])]}),"instanceName":"3"});
            var Q12;
            Q12=makeQuery(id+"F12.opPattern","COPY",BODY,{"derivedFrom":makeQuery(id+"F10.opExtrude","SWEPT_BODY",BODY,{"disambiguationData":[OSD([sQuery(id+"F9.wireOp",EDGE,"E19")])]}),"instanceName":"4"});
            var Q13;
            Q13=makeQuery(id+"F12.opPattern","COPY",BODY,{"derivedFrom":makeQuery(id+"F10.opExtrude","SWEPT_BODY",BODY,{"disambiguationData":[OSD([sQuery(id+"F9.wireOp",EDGE,"E19")])]}),"instanceName":"5"});
            var Q14;
            Q14=makeQuery(id+"F12.opPattern","COPY",BODY,{"derivedFrom":makeQuery(id+"F10.opExtrude","SWEPT_BODY",BODY,{"disambiguationData":[OSD([sQuery(id+"F9.wireOp",EDGE,"E19")])]}),"instanceName":"6"});
            var Q15;
            Q15=makeQuery(id+"F12.opPattern","COPY",BODY,{"derivedFrom":makeQuery(id+"F10.opExtrude","SWEPT_BODY",BODY,{"disambiguationData":[OSD([sQuery(id+"F9.wireOp",EDGE,"E19")])]}),"instanceName":"7"});
            var Q16;
            Q16=makeQuery(id+"F12.opPattern","COPY",BODY,{"derivedFrom":makeQuery(id+"F10.opExtrude","SWEPT_BODY",BODY,{"disambiguationData":[OSD([sQuery(id+"F9.wireOp",EDGE,"E19")])]}),"instanceName":"8"});
            var Q17;
            Q17=makeQuery(id+"F1.opExtrude","SWEPT_FACE",FACE,{"disambiguationData":[OSD([sQuery(id+"F0.wireOp",EDGE,"E0")])]});
            circularPattern(context, id + "F13", {"operationType" : NewBodyOperationType.ADD, "entities" : qUnion([Q0, Q1, Q2, Q3, Q4, Q5, Q6, Q7, Q8, Q9, Q10, Q11, Q12, Q13, Q14, Q15, Q16]), "axis" : qUnion([Q17]), "angle" : 360 * degree, "instanceCount" : 3, "equalSpace" : true});
        }
    });
